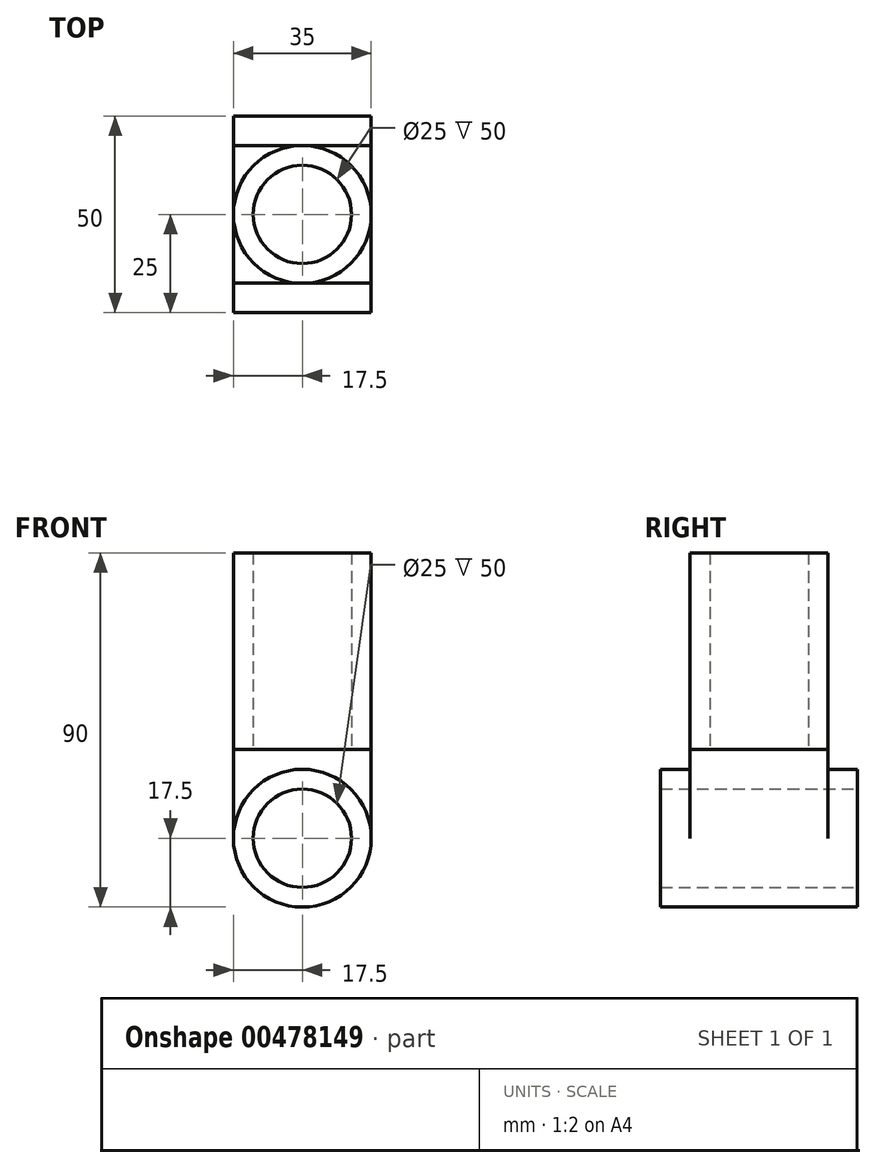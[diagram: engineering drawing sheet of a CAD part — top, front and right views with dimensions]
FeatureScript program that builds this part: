
annotation { "Feature Type Name" : "Feature", "Feature Type Description" : "" }
export const myFeature = defineFeature(function(context is Context, id is Id, definition is map)
    precondition{}
    {
        {
            var Q0;
            Q0=qCreatedBy(makeId("Front.planeOp"),FACE);
            var sketch = newSketch(context, id + "F0", { "sketchPlane" : qUnion([Q0])});
            skCircle(sketch, "E0", {"center": v(0, 0) * mm, "radius": 12.5 * mm});
            skCircle(sketch, "E1", {"center": v(0, 0) * mm, "radius": 17.5 * mm});
            skSolve(sketch);
        }
        {
            var Q0;
            Q0=makeQuery(id+"F0.imprint","IMPRINT",FACE,{"disambiguationData":[TD([[makeQuery(id+"F0.imprint","IMPRINT",EDGE,{"derivedFrom":sQuery(id+"F0.wireOp",EDGE,"E0")}),-1.0]])]});
            extrude(context, id + "F1", {"entities" : qUnion([Q0]), "endBound" : BoundingType.SYMMETRIC, "depth" : 50 * mm});
        }
        {
            var Q0;
            Q0=qCreatedBy(makeId("Top.planeOp"),FACE);
            var sketch = newSketch(context, id + "F2", { "sketchPlane" : qUnion([Q0])});
            skLineSegment(sketch, "E2.bottom", {"start": v(17.5, 17.5) * mm, "end": v(-17.5, 17.5) * mm});
            skLineSegment(sketch, "E2.top", {"start": v(17.5, -17.5) * mm, "end": v(-17.5, -17.5) * mm});
            skLineSegment(sketch, "E2.left", {"start": v(17.5, 17.5) * mm, "end": v(17.5, -17.5) * mm});
            skLineSegment(sketch, "E2.right", {"start": v(-17.5, 17.5) * mm, "end": v(-17.5, -17.5) * mm});
            skPoint(sketch, "E2.middle", {"position": v(0, 0) * mm});
            skSolve(sketch);
        }
        {
            var Q0;
            Q0 = qSketchRegion(id + "F2", true);
            extrude(context, id + "F3", {"entities" : qUnion([Q0]), "operationType" : NewBodyOperationType.ADD, "depth" : 22.5 * mm});
        }
        {
            var Q0;
            Q0=makeQuery(id+"F3.opExtrude","CAP_FACE",FACE,{"disambiguationData":[OSD([sQuery(id+"F2.wireOp",EDGE,"E2.bottom"),sQuery(id+"F2.wireOp",EDGE,"E2.top"),sQuery(id+"F2.wireOp",EDGE,"E2.left"),sQuery(id+"F2.wireOp",EDGE,"E2.right")])],"isStart":false});
            var sketch = newSketch(context, id + "F4", { "sketchPlane" : qUnion([Q0])});
            skCircle(sketch, "E3", {"center": v(0, 0) * mm, "radius": 12.5 * mm});
            skCircle(sketch, "E4", {"center": v(0, 0) * mm, "radius": 17.5 * mm});
            skSolve(sketch);
        }
        {
            var Q0;
            Q0=makeQuery(id+"F4.imprint","IMPRINT",FACE,{"disambiguationData":[TD([[makeQuery(id+"F4.imprint","IMPRINT",EDGE,{"derivedFrom":sQuery(id+"F4.wireOp",EDGE,"E3")}),-1.0]])]});
            extrude(context, id + "F5", {"entities" : qUnion([Q0]), "operationType" : NewBodyOperationType.ADD, "depth" : 50 * mm});
        }
        {
            var Q0;
            {var subQ0=sQuery(id+"F2.wireOp",EDGE,"E2.top");Q0=makeQuery(id+"F3.boolean.opBoolean","SPLIT",FACE,{"disambiguationData":[TD([makeQuery(id+"F1.opExtrude","SWEPT_FACE",FACE,{"disambiguationData":[OSD([sQuery(id+"F0.wireOp",EDGE,"E0")])]})])],"derivedFrom":makeQuery(id+"F3.opExtrude","SWEPT_FACE",FACE,{"disambiguationData":[OSD([subQ0])]})});}
            extrude(context, id + "F6", {"entities" : qUnion([Q0]), "operationType" : NewBodyOperationType.REMOVE, "endBound" : BoundingType.UP_TO_NEXT, "oppositeDirection" : true, "depth" : 25 * mm});
        }
    });
